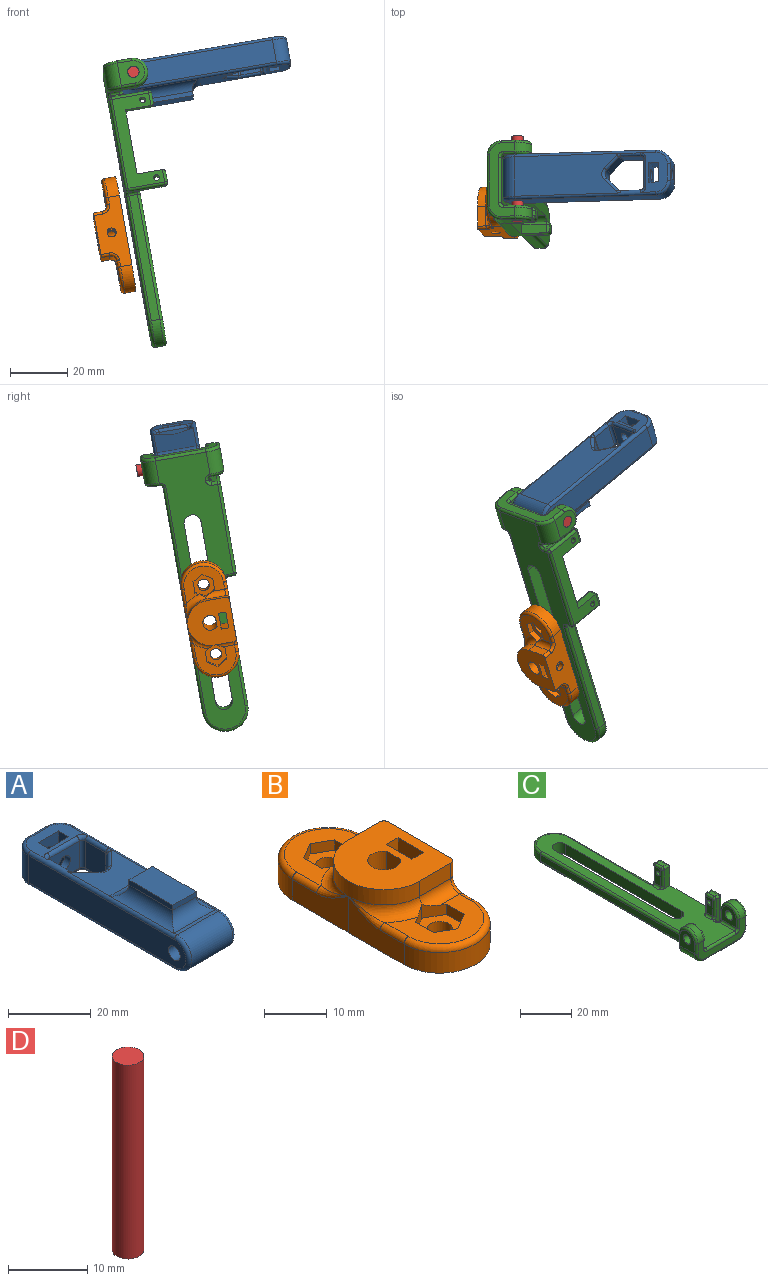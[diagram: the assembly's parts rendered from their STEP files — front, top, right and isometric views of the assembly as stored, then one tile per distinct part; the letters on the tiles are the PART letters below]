
ASSEMBLY  parts=4 mates=1
PART A: 71 faces, bbox 16.8x67.4x15.4 mm
  f0: plane 14x0.99mm, normal (0,0,1), area 13.9mm2, adj f45,f52,f58,f69
  f1: plane 14.41x14mm, normal (0,0,1), area 143.3mm2, adj f45,f47,f48,f49,f50,f51,f58,f64
  f2: plane 37.4x14mm, normal (0,0,-1), area 465.2mm2, adj f31,f32,f37,f38,f39,f42,f52,f62
  f3: plane 14x9.5mm, normal (0,0,1), area 75.3mm2, adj f12,f13,f14,f16,f35,f40,f41,f45
  f4: plane 8x4.29mm, normal (0.71,0.71,0), area 48.6mm2, adj f27,f38,f46,f50
  f5: plane 8x7.09mm, normal (1,0,0), area 56.7mm2, adj f36,f37,f45,f46
  f6: plane 10x8mm, normal (0,-1,0), area 67.4mm2, adj f26,f28,f34,f35,f36
  f7: plane 8x7.09mm, normal (-1,0,0), area 56.7mm2, adj f33,f34,f43,f44
  f8: plane 53.99x8mm, normal (-1,0,0), area 412.5mm2, adj f15,f19,f37,f45,f54
  f9: plane 53.99x8mm, normal (1,0,0), area 412.5mm2, adj f10,f19,f58,f60,f62
  f10: cylinder r=5mm len=8mm, axis (0,0,-1), area 62.8mm2, adj f9,f11,f56,f61
  f11: plane 8x6mm, normal (0,1,0), area 35.4mm2, adj f10,f15,f25,f55,f59
  f12: plane 10x7mm, normal (0,1,0), area 57.4mm2, adj f3,f13,f16,f18,f26
  f13: plane 10x3.5mm, normal (1,0,0), area 35mm2, adj f3,f12,f14,f18
  f14: plane 10x7mm, normal (0,-1,0), area 57.4mm2, adj f3,f13,f16,f18,f25
  f15: cylinder r=5mm len=8mm, axis (0,0,-1), area 62.8mm2, adj f8,f11,f53,f57
  f16: plane 10x3.5mm, normal (-1,0,0), area 35mm2, adj f3,f12,f14,f18
  f17: plane 8x4.29mm, normal (-0.71,0.71,0), area 48.6mm2, adj f27,f32,f43,f49
  f18: plane 14x9.5mm, normal (0,0,-1), area 75.3mm2, adj f12,f13,f14,f16,f28,f29,f30,f37
  f19: cylinder r=2mm len=16mm, axis (1,0,0), area 201.1mm2, adj f8,f9
  f20: plane 8x1.5mm, normal (0,-1,0), area 12mm2, adj f21,f23,f24,f69
  f21: plane 15x1.53mm, normal (1,0,0), area 22.9mm2, adj f20,f22,f24,f64,f68,f69
  f22: plane 8x1.5mm, normal (0,1,0), area 12mm2, adj f21,f23,f24,f64
  f23: plane 15x1.53mm, normal (-1,0,0), area 22.9mm2, adj f20,f22,f24,f64,f67,f69
  f24: plane 15x8mm, normal (0,0,1), area 120mm2, adj f20,f21,f22,f23
  f25: cylinder r=2mm len=4mm, axis (0,1,0), area 50.3mm2, adj f11,f14
  f26: cylinder r=2mm len=4mm, axis (0,1,0), area 25.1mm2, adj f6,f12
  f27: cylinder r=2mm len=8mm, axis (0,0,1), area 25.1mm2, adj f4,f17,f31,f51
  f28: cylinder r=1mm len=10mm, axis (1,0,0), area 15.7mm2, adj f6,f18,f29,f30
  f29: torus R=2mm, axis (0,0,1), area 3.4mm2, adj f18,f28,f33,f34
  f30: torus R=2mm, axis (0,0,1), area 3.4mm2, adj f18,f28,f36,f37
  f31: torus R=3mm, axis (0,0,1), area 5.8mm2, adj f2,f27,f32,f38
  f32: cylinder r=1mm len=5mm, axis (-0.71,-0.71,0), area 9.5mm2, adj f2,f17,f31,f39
  f33: cylinder r=1mm len=7.09mm, axis (0,-1,0), area 11.1mm2, adj f7,f29,f39,f62
  f34: cylinder r=1mm len=8mm, axis (0,0,1), area 12.6mm2, adj f6,f7,f29,f40
  f35: cylinder r=1mm len=10mm, axis (-1,0,0), area 15.7mm2, adj f3,f6,f40,f41
  f36: cylinder r=1mm len=8mm, axis (0,0,1), area 12.6mm2, adj f5,f6,f30,f41
  f37: cylinder r=1mm len=49.99mm, axis (0,1,0), area 89.7mm2, adj f2,f5,f8,f18,f30,f42,f54,f57
  f38: cylinder r=1mm len=5mm, axis (-0.71,0.71,0), area 9.5mm2, adj f2,f4,f31,f42
  f39: torus R=2mm, axis (0,0,1), area 1.7mm2, adj f2,f32,f33,f43
  f40: torus R=2mm, axis (0,0,1), area 3.4mm2, adj f3,f34,f35,f44
  f41: torus R=2mm, axis (0,0,1), area 3.4mm2, adj f3,f35,f36,f45
  f42: torus R=2mm, axis (0,0,1), area 1.7mm2, adj f2,f37,f38,f46
  f43: cylinder r=1mm len=8mm, axis (0,0,1), area 6.3mm2, adj f7,f17,f39,f47
  f44: cylinder r=1mm len=7.09mm, axis (0,1,0), area 11.1mm2, adj f7,f40,f47,f58
  f45: cylinder r=1mm len=49.99mm, axis (0,-1,0), area 87.2mm2, adj f0,f1,f3,f5,f8,f41,f48,f53
  f46: cylinder r=1mm len=8mm, axis (0,0,1), area 6.3mm2, adj f4,f5,f42,f48
  f47: torus R=2mm, axis (0,0,1), area 1.7mm2, adj f1,f43,f44,f49
  f48: torus R=2mm, axis (0,0,1), area 1.7mm2, adj f1,f45,f46,f50
  f49: cylinder r=1mm len=5mm, axis (0.71,0.71,0), area 9.5mm2, adj f1,f17,f47,f51
  f50: cylinder r=1mm len=5mm, axis (0.71,-0.71,0), area 9.5mm2, adj f1,f4,f48,f51
  f51: torus R=3mm, axis (0,0,1), area 5.8mm2, adj f1,f27,f49,f50
  f52: cylinder r=5mm len=14mm, axis (-1,0,0), area 219.9mm2, adj f0,f2,f54,f60
  f53: torus R=4mm, axis (0,0,1), area 11.4mm2, adj f3,f15,f45,f55
  f54: torus R=4mm, axis (-1,0,0), area 22.9mm2, adj f8,f37,f45,f52
  f55: cylinder r=1mm len=6mm, axis (1,0,0), area 9.4mm2, adj f3,f11,f53,f56
  f56: torus R=4mm, axis (0,0,1), area 11.4mm2, adj f3,f10,f55,f58
  f57: torus R=4mm, axis (0,0,1), area 11.4mm2, adj f15,f18,f37,f59
  f58: cylinder r=1mm len=49.99mm, axis (0,-1,0), area 76.1mm2, adj f0,f1,f3,f9,f44,f56,f60,f65
  f59: cylinder r=1mm len=6mm, axis (-1,0,0), area 9.4mm2, adj f11,f18,f57,f61
  f60: torus R=4mm, axis (-1,0,0), area 22.9mm2, adj f9,f52,f58,f62
  f61: torus R=4mm, axis (0,0,1), area 11.4mm2, adj f10,f18,f59,f62
  f62: cylinder r=1mm len=49.99mm, axis (0,1,0), area 78.5mm2, adj f2,f9,f18,f33,f60,f61
  f63: torus R=4.5mm, axis (0,1,0), area 0mm2, adj f45,f64,f67
  f64: cylinder r=3.5mm len=14mm, axis (1,0,0), area 57.3mm2, adj f1,f21,f22,f23,f63,f65,f67,f68
  f65: torus R=4.5mm, axis (0,1,0), area 0mm2, adj f58,f64,f68
  f66: torus R=4.5mm, axis (0,1,0), area 0mm2, adj f45,f67,f69
  f67: cylinder r=3.5mm len=22mm, axis (0,-1,0), area 88.5mm2, adj f23,f45,f63,f64,f66,f69
  f68: bspline ~57x3.48mm, area 88.5mm2, adj f21,f58,f64,f65,f69,f70
  f69: cylinder r=3.5mm len=14mm, axis (-1,0,0), area 57.3mm2, adj f0,f20,f21,f23,f66,f67,f68,f70
  f70: torus R=4.5mm, axis (0,1,0), area 0mm2, adj f58,f68,f69
PART B: 55 faces, bbox 21.3x42.6x10.3 mm
  f0: plane 14x12.36mm, normal (0,0,1), area 79.6mm2, adj f32,f33,f34,f35,f36,f37,f41,f42
  f1: plane 14x12.36mm, normal (0,0,1), area 79.6mm2, adj f25,f26,f27,f28,f29,f30,f39,f40
  f2: plane 4.54x3.07mm, normal (-1,0,0), area 11.3mm2, adj f12,f20,f24
  f3: plane 4.54x3.07mm, normal (-1,0,0), area 11.3mm2, adj f12,f17,f24
  f4: plane 10x5.7mm, normal (1,0,0), area 49mm2, adj f5,f16,f17,f20,f24
  f5: plane 10x2.6mm, normal (0,-1,0), area 26mm2, adj f4,f6,f17,f20
  f6: plane 10x5.7mm, normal (-1,0,0), area 49mm2, adj f5,f16,f17,f20,f21
  f7: plane 25x10mm, normal (1,0,0), area 179.8mm2, adj f8,f13,f17,f20,f21,f46,f47,f48
  f8: cylinder r=8mm len=16mm, axis (0,0,1), area 100.1mm2, adj f7,f9,f17,f45
  f9: plane 12.53x6.99mm, normal (-1,0,0), area 57.8mm2, adj f8,f10,f17,f43,f44
  f10: cylinder r=8mm len=16mm, axis (0,0,1), area 76.4mm2, adj f9,f11,f17,f18,f19,f20,f40,f41
  f11: plane 12.43x6.99mm, normal (-1,0,0), area 57.4mm2, adj f10,f13,f17,f49,f50
  f12: cylinder r=2.6mm len=10mm, axis (0,0,1), area 130.6mm2, adj f2,f3,f17,f20,f22,f23
  f13: cylinder r=8mm len=16mm, axis (0,0,1), area 100.5mm2, adj f7,f11,f17,f51
  f14: cylinder r=2mm len=4mm, axis (0,0,1), area 37.7mm2, adj f17,f38
  f15: cylinder r=2mm len=4mm, axis (0,0,1), area 37.7mm2, adj f17,f31
  f16: plane 10x2.6mm, normal (0,1,0), area 26mm2, adj f4,f6,f17,f20
  f17: plane 41x16mm, normal (0,0,-1), area 540.9mm2, adj f3,f4,f5,f6,f7,f8,f9,f10
  f18: plane 7x3mm, normal (0,1,0), area 21mm2, adj f10,f20,f42,f48
  f19: plane 7x3mm, normal (0,-1,0), area 21mm2, adj f10,f20,f39,f54
  f20: plane 16x16mm, normal (0,0,1), area 193.1mm2, adj f2,f4,f5,f6,f7,f10,f12,f16
  f21: cylinder r=1.6mm len=3.2mm, axis (1,0,0), area 20.1mm2, adj f6,f7
  f22: plane 0.92x0.07mm, normal (1,0,0), area 0mm2, adj f12,f24
  f23: plane 0.92x0.07mm, normal (1,0,0), area 0mm2, adj f12,f24
  f24: cylinder r=1.6mm len=3.2mm, axis (1,0,0), area 13.1mm2, adj f2,f3,f4,f22,f23
  f25: plane 3.6x2.83mm, normal (0.5,-0.87,0), area 8.7mm2, adj f1,f26,f30,f31,f40
  f26: plane 4.04x2mm, normal (1,0,0), area 8.1mm2, adj f1,f25,f27,f31
  f27: plane 3.5x2.02mm, normal (0.5,0.87,0), area 8.1mm2, adj f1,f26,f28,f31
  f28: plane 3.5x2.02mm, normal (-0.5,0.87,0), area 8.1mm2, adj f1,f27,f29,f31
  f29: plane 4.04x2mm, normal (-1,0,0), area 8.1mm2, adj f1,f28,f30,f31
  f30: plane 3.79x3.01mm, normal (-0.5,-0.87,0), area 8.8mm2, adj f1,f25,f29,f31,f39
  f31: plane 8.08x7mm, normal (0,0,1), area 29.9mm2, adj f15,f25,f26,f27,f28,f29,f30
  f32: plane 3.79x3.01mm, normal (-0.5,0.87,0), area 8.8mm2, adj f0,f33,f37,f38,f42
  f33: plane 4.04x2mm, normal (-1,0,0), area 8.1mm2, adj f0,f32,f34,f38
  f34: plane 3.5x2.02mm, normal (-0.5,-0.87,0), area 8.1mm2, adj f0,f33,f35,f38
  f35: plane 3.5x2.02mm, normal (0.5,-0.87,0), area 8.1mm2, adj f0,f34,f36,f38
  f36: plane 4.04x2mm, normal (1,0,0), area 8.1mm2, adj f0,f35,f37,f38
  f37: plane 3.6x2.83mm, normal (0.5,0.87,0), area 8.7mm2, adj f0,f32,f36,f38,f41
  f38: plane 8.08x7mm, normal (0,0,1), area 29.9mm2, adj f14,f32,f33,f34,f35,f36,f37
  f39: cylinder r=2mm len=7mm, axis (1,0,0), area 19.6mm2, adj f1,f19,f30,f40,f53
  f40: torus R=10mm, axis (0,0,1), area 28.4mm2, adj f1,f10,f25,f39,f49
  f41: torus R=10mm, axis (0,0,1), area 28.4mm2, adj f0,f10,f37,f42,f43
  f42: cylinder r=2mm len=7mm, axis (-1,0,0), area 19.6mm2, adj f0,f18,f32,f41,f47
  f43: bspline ~8.08x3mm, area 6.1mm2, adj f9,f10,f41,f44
  f44: cylinder r=1mm len=5.46mm, axis (0,1,0), area 8.6mm2, adj f0,f9,f43,f45
  f45: torus R=7mm, axis (0,0,1), area 37.5mm2, adj f0,f8,f44,f46
  f46: cylinder r=1mm len=2.5mm, axis (0,1,0), area 3.9mm2, adj f0,f7,f45,f47
  f47: torus R=3mm, axis (-1,0,0), area 5.8mm2, adj f7,f42,f46,f48
  f48: cylinder r=1mm len=3mm, axis (0,0,1), area 4.7mm2, adj f7,f18,f20,f47
  f49: bspline ~8.08x3mm, area 6.1mm2, adj f10,f11,f40,f50
  f50: cylinder r=1mm len=5.36mm, axis (0,-1,0), area 8.4mm2, adj f1,f11,f49,f51
  f51: torus R=7mm, axis (0,0,1), area 37.7mm2, adj f1,f13,f50,f52
  f52: cylinder r=1mm len=2.5mm, axis (0,1,0), area 3.9mm2, adj f1,f7,f51,f53
  f53: torus R=3mm, axis (-1,0,0), area 5.8mm2, adj f7,f39,f52,f54
  f54: cylinder r=1mm len=3mm, axis (0,0,-1), area 4.7mm2, adj f7,f19,f20,f53
PART C: 110 faces, bbox 28.9x101.1x15.9 mm
  f0: plane 98.05x20.03mm, normal (0,0,1), area 1074.2mm2, adj f1,f2,f3,f8,f15,f20,f23,f37
  f1: cylinder r=3mm len=6mm, axis (0,0,-1), area 47.3mm2, adj f0,f2,f15,f16
  f2: plane 63.98x5mm, normal (1,0,0), area 319.9mm2, adj f0,f1,f3,f16
  f3: cylinder r=3mm len=6mm, axis (0,0,-1), area 47.2mm2, adj f0,f2,f15,f16
  f4: plane 26x9mm, normal (0,-1,0), area 108.8mm2, adj f25,f26,f71,f72,f73,f74,f75,f91
  f5: plane 9x8mm, normal (1,0,0), area 52.6mm2, adj f27,f29,f75,f76,f77
  f6: plane 9x3.99mm, normal (0,1,0), area 27.2mm2, adj f26,f33,f77,f78,f97,f98
  f7: plane 13.03x2.64mm, normal (0,-1,0), area 26.4mm2, adj f34,f47,f49,f50,f101,f103,f104
  f8: plane 32.03x13mm, normal (1,0,0), area 202.8mm2, adj f0,f20,f23,f31,f32,f45,f55,f104
  f9: plane 13.03x2.64mm, normal (0,1,0), area 26.4mm2, adj f35,f51,f52,f53,f61,f82,f108
  f10: plane 45.01x3mm, normal (1,0,0), area 135mm2, adj f11,f35,f63,f83
  f11: cylinder r=8mm len=16mm, axis (0,0,-1), area 75.8mm2, adj f10,f12,f64,f84
  f12: plane 80.87x3mm, normal (-1,0,0), area 242.6mm2, adj f11,f36,f65,f85
  f13: plane 9x4mm, normal (0,1,0), area 27.4mm2, adj f25,f36,f67,f68,f69,f88,f89
  f14: plane 9x8mm, normal (-1,0,0), area 52.6mm2, adj f28,f30,f69,f70,f71
  f15: plane 63.98x5mm, normal (-1,0,0), area 319.9mm2, adj f0,f1,f3,f16
  f16: plane 98.02x20.01mm, normal (0,0,-1), area 1103mm2, adj f1,f2,f3,f15,f27,f28,f61,f62
  f17: plane 8x8mm, normal (1,0,0), area 44.6mm2, adj f30,f40,f89,f90,f91
  f18: plane 8x8mm, normal (-1,0,0), area 44.6mm2, adj f29,f39,f95,f96,f97
  f19: plane 8x3.5mm, normal (-1,0,0), area 24.9mm2, adj f32,f38,f42,f46,f49
  f20: plane 9x3.27mm, normal (0,1,0), area 27.1mm2, adj f0,f8,f41,f42,f43
  f21: plane 3.5x2mm, normal (0,0,1), area 7mm2, adj f43,f45,f46,f47
  f22: plane 8x3.5mm, normal (-1,0,0), area 24.9mm2, adj f31,f37,f52,f56,f59
  f23: plane 9x3.27mm, normal (0,-1,0), area 27.1mm2, adj f0,f8,f57,f59,f60
  f24: plane 3.5x2mm, normal (0,0,1), area 7mm2, adj f53,f55,f56,f57
  f25: cylinder r=5mm len=10mm, axis (-1,0,0), area 47.4mm2, adj f4,f13,f70,f90
  f26: cylinder r=5mm len=10mm, axis (1,0,0), area 46.8mm2, adj f4,f6,f76,f96
  f27: cylinder r=5mm len=8mm, axis (0,1,0), area 62.8mm2, adj f5,f16,f74,f78,f79
  f28: cylinder r=5mm len=8mm, axis (0,-1,0), area 62.8mm2, adj f14,f16,f68,f72
  f29: cylinder r=2mm len=4.98mm, axis (-1,0,0), area 62.6mm2, adj f5,f18
  f30: cylinder r=2mm len=5.02mm, axis (-1,0,0), area 63.1mm2, adj f14,f17
  f31: cylinder r=1mm len=4mm, axis (-1,0,0), area 25.1mm2, adj f8,f22
  f32: cylinder r=1mm len=4mm, axis (-1,0,0), area 25.1mm2, adj f8,f19
  f33: cylinder r=1mm len=3.26mm, axis (0,0,-1), area 4.7mm2, adj f6,f34,f79,f80,f99,f100
  f34: cylinder r=1mm len=3mm, axis (0,0,1), area 4.7mm2, adj f7,f33,f81,f101
  f35: cylinder r=1mm len=3mm, axis (0,0,1), area 4.7mm2, adj f9,f10,f62,f82
  f36: cylinder r=1mm len=3.28mm, axis (0,0,1), area 4.8mm2, adj f12,f13,f66,f86,f87
  f37: cylinder r=1mm len=3.5mm, axis (0,1,0), area 5.5mm2, adj f0,f22,f51,f60
  f38: cylinder r=1mm len=3.5mm, axis (0,1,0), area 5.5mm2, adj f0,f19,f41,f50
  f39: cylinder r=1mm len=8.26mm, axis (0,1,0), area 12.6mm2, adj f0,f18,f94,f98,f99
  f40: cylinder r=1mm len=8.28mm, axis (0,-1,0), area 12.6mm2, adj f0,f17,f87,f88,f92
  f41: torus R=2mm, axis (0,1,0), area 1.9mm2, adj f0,f20,f38,f42
  f42: cylinder r=1mm len=8mm, axis (0,0,-1), area 12.6mm2, adj f19,f20,f41,f44
  f43: cylinder r=1mm len=3mm, axis (1,0,0), area 4.1mm2, adj f20,f21,f44,f45
  f44: sphere r=1mm, area 1.6mm2, adj f42,f43,f46
  f45: cylinder r=1mm len=4.5mm, axis (0,-1,0), area 6.5mm2, adj f8,f21,f43,f102
  f46: cylinder r=1mm len=3.5mm, axis (0,1,0), area 5.5mm2, adj f19,f21,f44,f48
  f47: cylinder r=1mm len=2mm, axis (-1,0,0), area 3.1mm2, adj f7,f21,f48,f102
  f48: sphere r=1mm, area 1.6mm2, adj f46,f47,f49
  f49: cylinder r=1mm len=8mm, axis (0,0,1), area 12.6mm2, adj f7,f19,f48,f50
  f50: torus R=2mm, axis (0,1,0), area 2.1mm2, adj f0,f7,f38,f49,f101
  f51: torus R=2mm, axis (0,-1,0), area 2.1mm2, adj f0,f9,f37,f52,f82
  f52: cylinder r=1mm len=8mm, axis (0,0,-1), area 12.6mm2, adj f9,f22,f51,f54
  f53: cylinder r=1mm len=2mm, axis (1,0,0), area 3.1mm2, adj f9,f24,f54,f109
  f54: sphere r=1mm, area 1.6mm2, adj f52,f53,f56
  f55: cylinder r=1mm len=4.5mm, axis (0,-1,0), area 6.5mm2, adj f8,f24,f57,f109
  f56: cylinder r=1mm len=3.5mm, axis (0,1,0), area 5.5mm2, adj f22,f24,f54,f58
  f57: cylinder r=1mm len=3mm, axis (-1,0,0), area 4.1mm2, adj f23,f24,f55,f58
  f58: sphere r=1mm, area 1.6mm2, adj f56,f57,f59
  f59: cylinder r=1mm len=8mm, axis (0,0,-1), area 12.6mm2, adj f22,f23,f58,f60
  f60: torus R=2mm, axis (0,1,0), area 1.9mm2, adj f0,f23,f37,f59
  f61: cylinder r=1mm len=2mm, axis (-1,0,0), area 3.1mm2, adj f9,f16,f62,f107
  f62: torus R=2mm, axis (0,0,1), area 3.4mm2, adj f16,f35,f61,f63
  f63: cylinder r=1mm len=45.01mm, axis (0,1,0), area 70.7mm2, adj f10,f16,f62,f64
  f64: torus R=7mm, axis (0,0,1), area 37.9mm2, adj f11,f16,f63,f65
  f65: cylinder r=1mm len=80.88mm, axis (0,-1,0), area 127mm2, adj f12,f16,f64,f66
  f66: torus R=2mm, axis (0,0,1), area 3.4mm2, adj f16,f36,f65,f67
  f67: cylinder r=1mm len=1mm, axis (-1,0,0), area 0mm2, adj f13,f16,f66,f68
  f68: torus R=4mm, axis (0,1,0), area 11.4mm2, adj f13,f28,f67,f69
  f69: cylinder r=1mm len=5mm, axis (0,0,1), area 7.9mm2, adj f13,f14,f68,f70
  f70: torus R=4mm, axis (1,0,0), area 22.9mm2, adj f14,f25,f69,f71
  f71: cylinder r=1mm len=5mm, axis (0,0,-1), area 7.9mm2, adj f4,f14,f70,f72
  f72: torus R=4mm, axis (0,1,0), area 11.4mm2, adj f4,f28,f71,f73
  f73: cylinder r=1mm len=18mm, axis (1,0,0), area 28.3mm2, adj f4,f16,f72,f74
  f74: torus R=4mm, axis (0,1,0), area 11.4mm2, adj f4,f27,f73,f75
  f75: cylinder r=1mm len=5mm, axis (0,0,1), area 7.9mm2, adj f4,f5,f74,f76
  f76: torus R=4mm, axis (1,0,0), area 22.9mm2, adj f5,f26,f75,f77
  f77: cylinder r=1mm len=5mm, axis (0,0,-1), area 7.9mm2, adj f5,f6,f76,f78
  f78: torus R=4mm, axis (0,1,0), area 11.4mm2, adj f6,f27,f77,f79
  f79: bspline ~1x1mm, area 0mm2, adj f27,f33,f78,f80
  f80: torus R=2mm, axis (0,0,1), area 3.3mm2, adj f16,f33,f79,f81
  f81: torus R=2mm, axis (0,0,1), area 3.3mm2, adj f16,f34,f80,f103
  f82: torus R=2mm, axis (0,0,1), area 2.1mm2, adj f0,f9,f35,f51,f83
  f83: cylinder r=1mm len=45.01mm, axis (0,-1,0), area 70.7mm2, adj f0,f10,f82,f84
  f84: torus R=7mm, axis (0,0,1), area 37.9mm2, adj f0,f11,f83,f85
  f85: cylinder r=1mm len=80.88mm, axis (0,1,0), area 127mm2, adj f0,f12,f84,f86
  f86: torus R=2mm, axis (0,0,1), area 2.2mm2, adj f0,f36,f85,f87
  f87: bspline ~1.26x1.23mm, area 0.7mm2, adj f36,f40,f86,f88
  f88: torus R=2mm, axis (0,1,0), area 2.2mm2, adj f13,f40,f87,f89
  f89: cylinder r=1mm len=4mm, axis (0,0,-1), area 6.3mm2, adj f13,f17,f88,f90
  f90: torus R=4mm, axis (1,0,0), area 22.9mm2, adj f17,f25,f89,f91
  f91: cylinder r=1mm len=4mm, axis (0,0,1), area 6.3mm2, adj f4,f17,f90,f92
  f92: torus R=2mm, axis (0,1,0), area 3.4mm2, adj f4,f40,f91,f93
  f93: cylinder r=1mm len=16mm, axis (-1,0,0), area 25.1mm2, adj f0,f4,f92,f94
  f94: torus R=2mm, axis (0,1,0), area 3.4mm2, adj f4,f39,f93,f95
  f95: cylinder r=1mm len=4mm, axis (0,0,-1), area 6.3mm2, adj f4,f18,f94,f96
  f96: torus R=4mm, axis (1,0,0), area 22.9mm2, adj f18,f26,f95,f97
  f97: cylinder r=1mm len=4mm, axis (0,0,1), area 6.3mm2, adj f6,f18,f96,f98
  f98: torus R=2mm, axis (0,1,0), area 2.3mm2, adj f6,f39,f97,f99
  f99: bspline ~1.34x1.25mm, area 0.7mm2, adj f33,f39,f98,f100
  f100: torus R=2mm, axis (0,0,1), area 2.2mm2, adj f0,f33,f99,f101
  f101: torus R=2mm, axis (0,0,1), area 2.1mm2, adj f0,f7,f34,f50,f100
  f102: sphere r=1mm, area 1.6mm2, adj f45,f47,f104
  f103: cylinder r=1mm len=2mm, axis (1,0,0), area 3.1mm2, adj f7,f16,f81,f105
  f104: cylinder r=1mm len=13mm, axis (0,0,-1), area 20.4mm2, adj f7,f8,f102,f105
  f105: sphere r=1mm, area 1.6mm2, adj f103,f104,f106
  f106: cylinder r=1mm len=32.03mm, axis (0,1,0), area 50.3mm2, adj f8,f16,f105,f107
  f107: sphere r=1mm, area 1.6mm2, adj f61,f106,f108
  f108: cylinder r=1mm len=13mm, axis (0,0,-1), area 20.4mm2, adj f8,f9,f107,f109
  f109: sphere r=1mm, area 1.6mm2, adj f53,f55,f108
PART D: 3 faces, bbox 4x4x30 mm
  f0: cylinder r=2mm len=30mm, axis (0,0,-1), area 377mm2, adj f1,f2
  f1: plane 4x4mm, normal (0,0,1), area 12.6mm2, adj f0
  f2: plane 4x4mm, normal (0,0,-1), area 12.6mm2, adj f0
PLACE A rot(axis=(0.7,0.71,0),165.9deg) t=(16.02,0.64,20)mm
PLACE B rot(axis=(0.58,-0.67,-0.47),120deg) t=(-16.19,-10.86,-39.16)mm
PLACE C rot(axis=(-0.58,0.47,-0.67),120deg) t=(-10.59,-9.07,-29.45)mm
PLACE D rot(axis=(0.61,0.51,-0.61),108.1deg) t=(-8.6,14.66,13.12)mm
MATE cylindrical C.f29 <-> D.f0  axis (0,-0.98,0.17) through (-8.6,-14.86,18.32)mm
